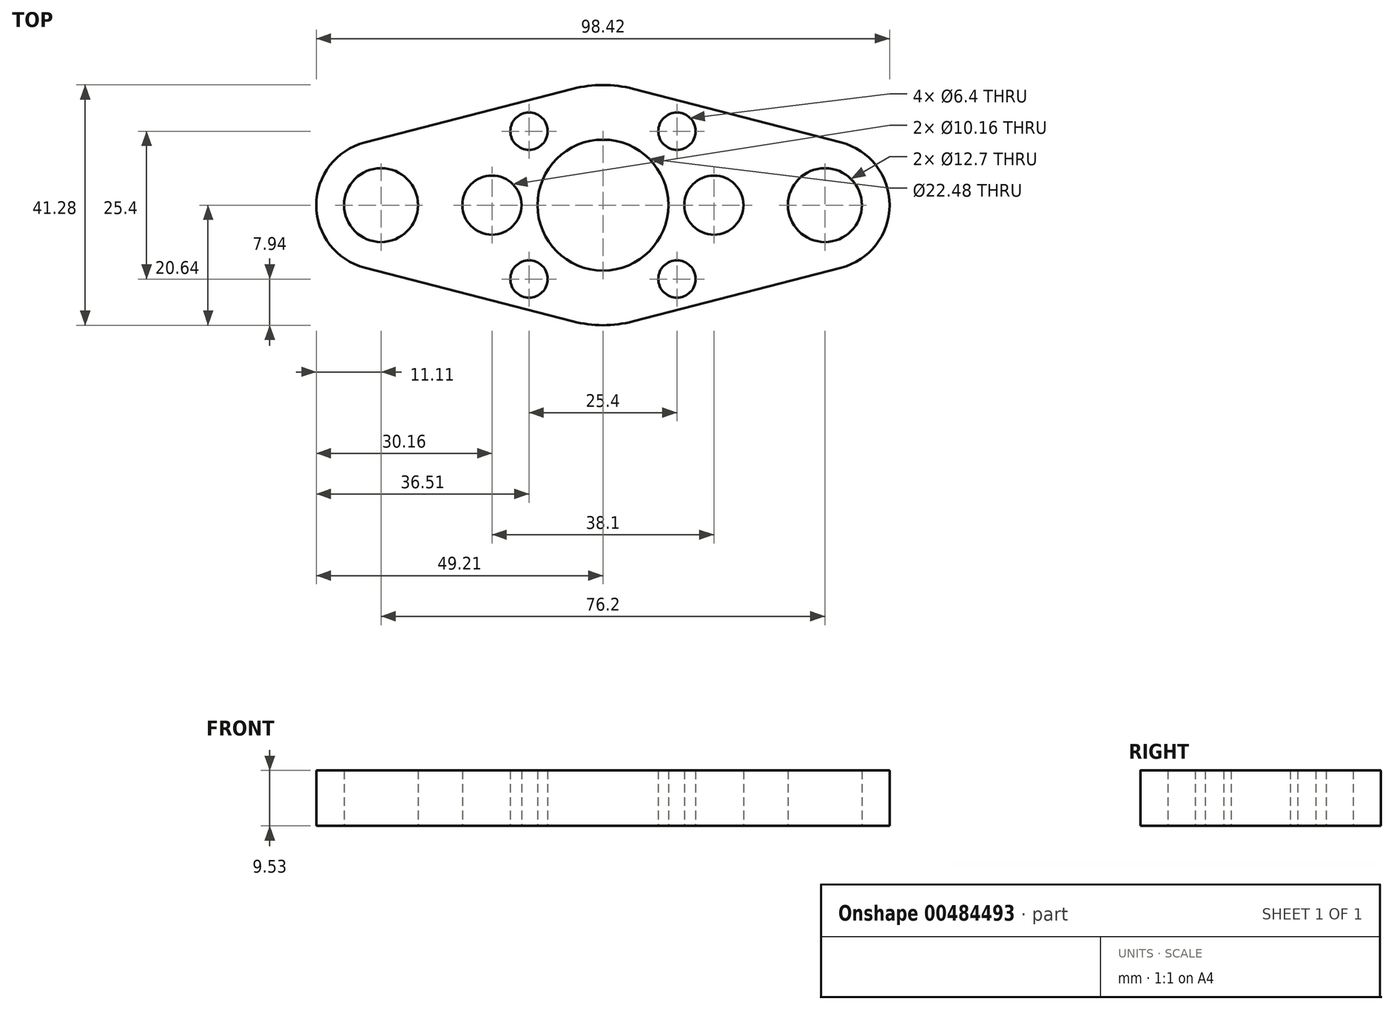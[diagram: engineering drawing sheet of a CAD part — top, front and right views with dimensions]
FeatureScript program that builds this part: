
annotation { "Feature Type Name" : "Feature", "Feature Type Description" : "" }
export const myFeature = defineFeature(function(context is Context, id is Id, definition is map)
    precondition{}
    {
        {
            var Q0;
            Q0=qCreatedBy(makeId("Top.planeOp"),FACE);
            var sketch = newSketch(context, id + "F0", { "sketchPlane" : qUnion([Q0])});
            skCircle(sketch, "E0", {"center": v(0, 0) * mm, "radius": 11.24 * mm});
            skCircle(sketch, "E1", {"center": v(-19.05, 0) * mm, "radius": 5.08 * mm});
            skCircle(sketch, "E2", {"center": v(19.05, 0) * mm, "radius": 5.08 * mm});
            skLineSegment(sketch, "E3", {"start": v(-19.05, 0) * mm, "end": v(19.05, 0) * mm, "construction": true});
            skCircle(sketch, "E4", {"center": v(-38.1, 0) * mm, "radius": 6.35 * mm});
            skCircle(sketch, "E5", {"center": v(38.1, 0) * mm, "radius": 6.35 * mm});
            skLineSegment(sketch, "E6", {"start": v(-19.05, 0) * mm, "end": v(-38.1, 0) * mm, "construction": true});
            skLineSegment(sketch, "E7", {"start": v(19.05, 0) * mm, "end": v(38.1, 0) * mm, "construction": true});
            skArc(sketch, "E8", {"start": v(-40.88, 10.76) * mm, "mid": v(-49.21, 0) * mm, "end": v(-40.88, -10.76) * mm});
            skArc(sketch, "E9", {"start": v(40.88, -10.76) * mm, "mid": v(49.21, 0) * mm, "end": v(40.88, 10.76) * mm});
            skArc(sketch, "E10", {"start": v(-5.16, -19.98) * mm, "mid": v(0, -20.64) * mm, "end": v(5.16, -19.98) * mm});
            skLineSegment(sketch, "E11", {"start": v(-40.88, 10.76) * mm, "end": v(-5.16, 19.98) * mm});
            skLineSegment(sketch, "E12", {"start": v(5.16, 19.98) * mm, "end": v(40.88, 10.76) * mm});
            skLineSegment(sketch, "E13", {"start": v(-40.88, -10.76) * mm, "end": v(-5.16, -19.98) * mm});
            skLineSegment(sketch, "E14", {"start": v(5.16, -19.98) * mm, "end": v(40.88, -10.76) * mm});
            skArc(sketch, "E15.trimOffspring", {"start": v(5.16, 19.98) * mm, "mid": v(0, 20.64) * mm, "end": v(-5.16, 19.98) * mm});
            skLineSegment(sketch, "E16.bottom", {"start": v(-12.7, 12.7) * mm, "end": v(12.7, 12.7) * mm, "construction": true});
            skLineSegment(sketch, "E16.top", {"start": v(-12.7, -12.7) * mm, "end": v(12.7, -12.7) * mm, "construction": true});
            skLineSegment(sketch, "E16.left", {"start": v(-12.7, 12.7) * mm, "end": v(-12.7, -12.7) * mm, "construction": true});
            skLineSegment(sketch, "E16.right", {"start": v(12.7, 12.7) * mm, "end": v(12.7, -12.7) * mm, "construction": true});
            skCircle(sketch, "E17", {"center": v(-12.7, 12.7) * mm, "radius": 3.2 * mm});
            skCircle(sketch, "E18", {"center": v(-12.7, -12.7) * mm, "radius": 3.2 * mm});
            skCircle(sketch, "E19", {"center": v(12.7, -12.7) * mm, "radius": 3.2 * mm});
            skCircle(sketch, "E20", {"center": v(12.7, 12.7) * mm, "radius": 3.2 * mm});
            skSolve(sketch);
        }
        {
            var Q0;
            Q0=qSketchRegion(id+"F0",true);
            extrude(context, id + "F1", {"entities" : qUnion([Q0]), "offsetDistance" : 25.4 * mm, "depth" : 9.52 * mm});
        }
    });
